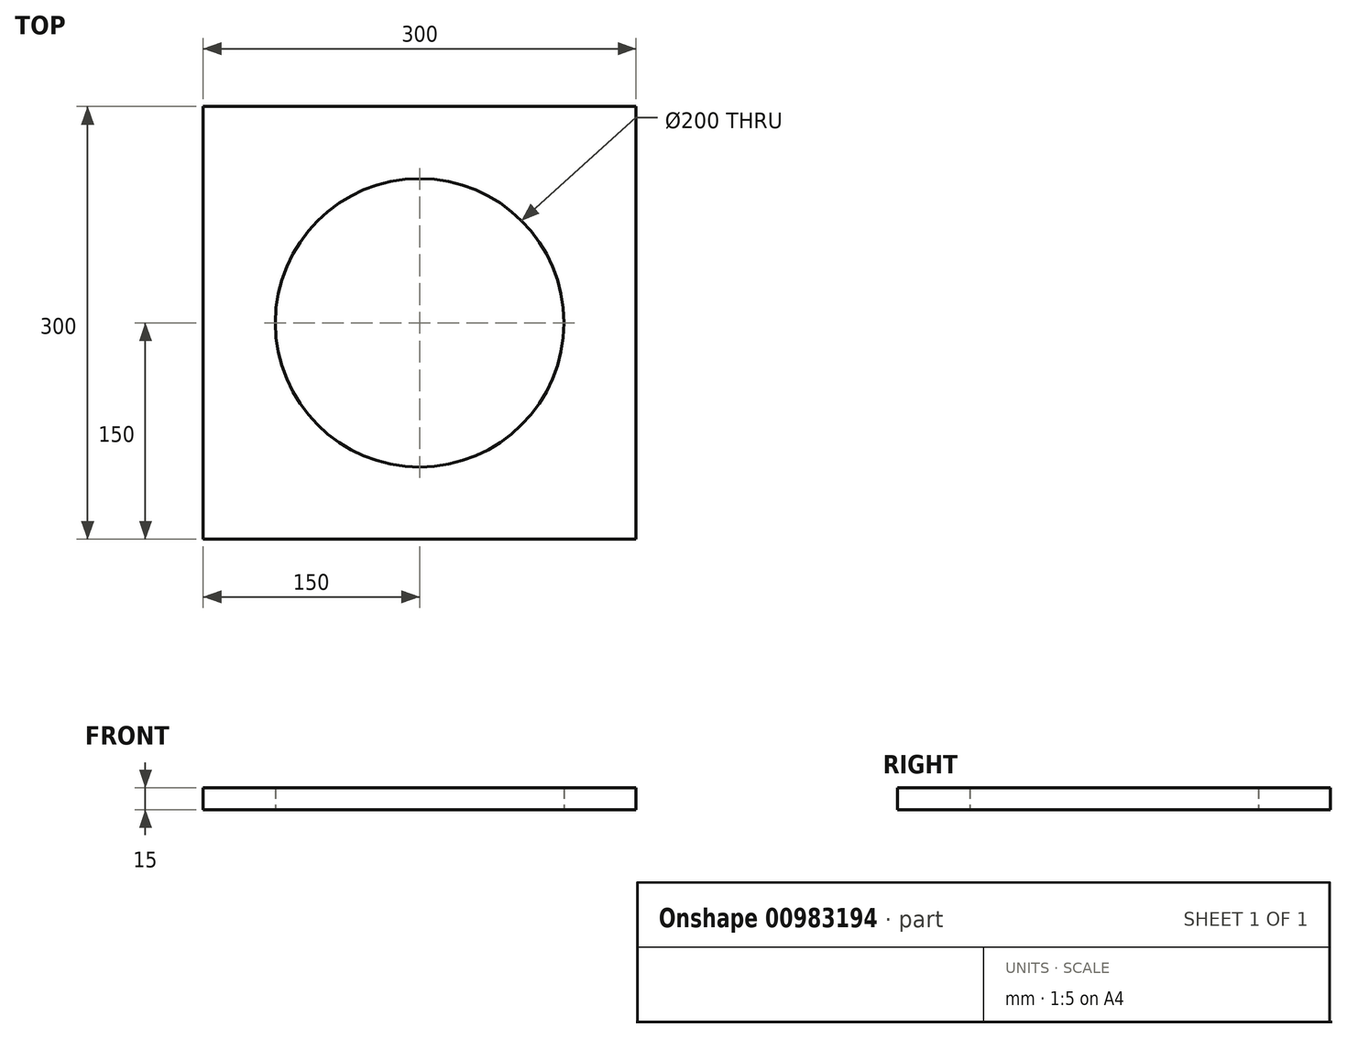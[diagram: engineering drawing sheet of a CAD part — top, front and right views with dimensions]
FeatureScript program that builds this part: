
annotation { "Feature Type Name" : "Feature", "Feature Type Description" : "" }
export const myFeature = defineFeature(function(context is Context, id is Id, definition is map)
    precondition{}
    {
        {
            var Q0;
            Q0=qCreatedBy(makeId("Top.planeOp"),FACE);
            var sketch = newSketch(context, id + "F0", { "sketchPlane" : qUnion([Q0])});
            skLineSegment(sketch, "E0.bottom", {"start": v(150, -150) * mm, "end": v(-150, -150) * mm});
            skLineSegment(sketch, "E0.top", {"start": v(150, 150) * mm, "end": v(-150, 150) * mm});
            skLineSegment(sketch, "E0.left", {"start": v(150, -150) * mm, "end": v(150, 150) * mm});
            skLineSegment(sketch, "E0.right", {"start": v(-150, -150) * mm, "end": v(-150, 150) * mm});
            skPoint(sketch, "E0.middle", {"position": v(0, 0) * mm});
            skCircle(sketch, "E1", {"center": v(0, 0) * mm, "radius": 100 * mm});
            skSolve(sketch);
        }
        {
            var Q0;
            Q0 = qSketchRegion(id + "F0", true);
            extrude(context, id + "F1", {"entities" : qUnion([Q0]), "depth" : 15 * mm, "offsetDistance" : 25 * mm});
        }
    });
